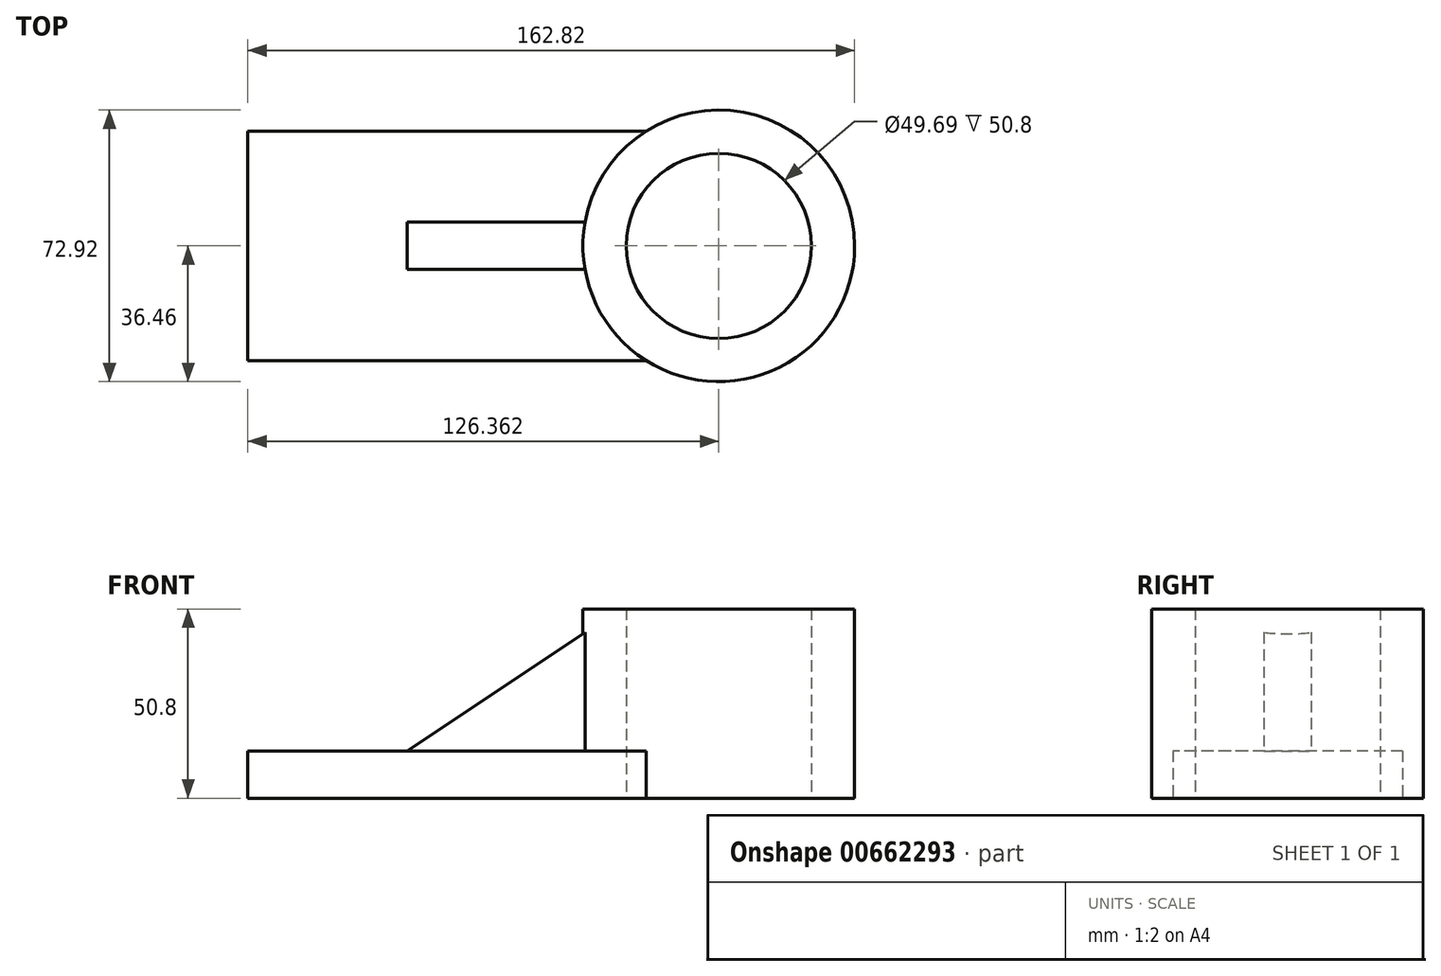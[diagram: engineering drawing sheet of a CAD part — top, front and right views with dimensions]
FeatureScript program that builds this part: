
annotation { "Feature Type Name" : "Feature", "Feature Type Description" : "" }
export const myFeature = defineFeature(function(context is Context, id is Id, definition is map)
    precondition{}
    {
        {
            var Q0;
            Q0=qCreatedBy(makeId("Top.planeOp"),FACE);
            var sketch = newSketch(context, id + "F0", { "sketchPlane" : qUnion([Q0])});
            skLineSegment(sketch, "E0.bottom", {"start": v(-63.18, 30.82) * mm, "end": v(43.7, 30.82) * mm});
            skLineSegment(sketch, "E0.top", {"start": v(-63.18, -30.82) * mm, "end": v(43.7, -30.82) * mm});
            skLineSegment(sketch, "E0.left", {"start": v(-63.18, 30.82) * mm, "end": v(-63.18, -30.82) * mm});
            skPoint(sketch, "E0.middle", {"position": v(0, 0) * mm});
            skCircle(sketch, "E1", {"center": v(63.18, 0) * mm, "radius": 36.46 * mm});
            skCircle(sketch, "E2", {"center": v(63.18, 0) * mm, "radius": 24.85 * mm});
            skPoint(sketch, "E3.orphan", {"position": v(63.18, 30.82) * mm});
            skPoint(sketch, "E4.start.orphan", {"position": v(63.18, -30.82) * mm});
            skSolve(sketch);
        }
        {
            var Q0;
            Q0=makeQuery(id+"F0.imprint","IMPRINT",FACE,{"disambiguationData":[TD([[makeQuery(id+"F0.imprint","IMPRINT",EDGE,{"derivedFrom":sQuery(id+"F0.wireOp",EDGE,"E2")}),-1.0]])]});
            extrude(context, id + "F1", {"entities" : qUnion([Q0]), "depth" : 50.8 * mm, "offsetDistance" : 25.4 * mm});
        }
        {
            var Q0;
            {var subQ0=sQuery(id+"F0.wireOp",EDGE,"E0.bottom");Q0=makeQuery(id+"F0.imprint","IMPRINT",FACE,{"disambiguationData":[TD([[makeQuery(id+"F0.imprint","IMPRINT",EDGE,{"derivedFrom":subQ0}),-1.0]])]});}
            extrude(context, id + "F2", {"entities" : qUnion([Q0]), "operationType" : NewBodyOperationType.ADD, "depth" : 12.7 * mm, "offsetDistance" : 25.4 * mm});
        }
        {
            var Q0;
            Q0=qCreatedBy(makeId("Front.planeOp"),FACE);
            var sketch = newSketch(context, id + "F3", { "sketchPlane" : qUnion([Q0])});
            skLineSegment(sketch, "E5", {"start": v(30.64, 46.75) * mm, "end": v(-22.83, 11.1) * mm});
            skLineSegment(sketch, "E6", {"start": v(-22.83, 11.1) * mm, "end": v(30.64, 11.1) * mm});
            skLineSegment(sketch, "E7", {"start": v(30.64, 11.1) * mm, "end": v(30.64, 46.75) * mm});
            skSolve(sketch);
        }
        {
            var Q0;
            Q0 = qSketchRegion(id + "F3", true);
            extrude(context, id + "F4", {"entities" : qUnion([Q0]), "operationType" : NewBodyOperationType.ADD, "endBound" : BoundingType.SYMMETRIC, "depth" : 12.7 * mm, "offsetDistance" : 25.4 * mm});
        }
    });
